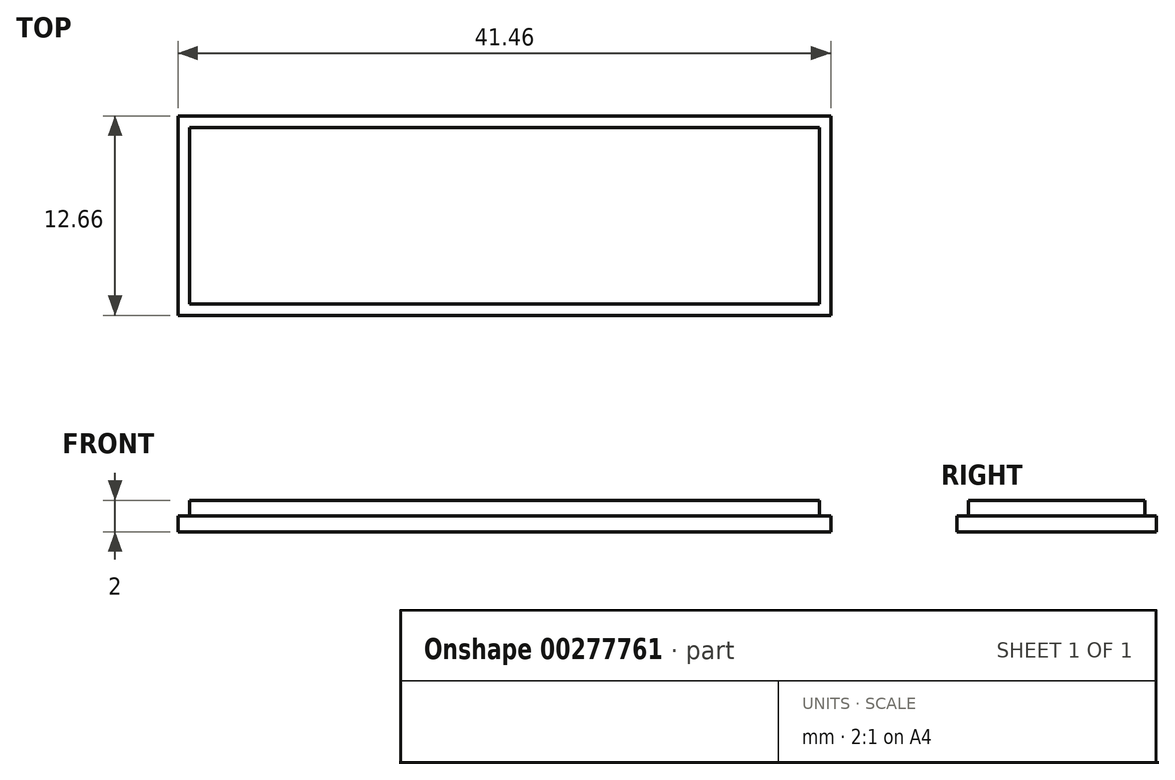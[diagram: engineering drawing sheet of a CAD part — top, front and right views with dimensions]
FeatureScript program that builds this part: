
annotation { "Feature Type Name" : "Feature", "Feature Type Description" : "" }
export const myFeature = defineFeature(function(context is Context, id is Id, definition is map)
    precondition{}
    {
        {
            var Q0;
            Q0=qCreatedBy(makeId("Top.planeOp"),FACE);
            var sketch = newSketch(context, id + "F0", { "sketchPlane" : qUnion([Q0])});
            skLineSegment(sketch, "E0.bottom", {"start": v(20.73, -6.33) * mm, "end": v(-20.73, -6.33) * mm});
            skLineSegment(sketch, "E0.top", {"start": v(20.73, 6.33) * mm, "end": v(-20.73, 6.33) * mm});
            skLineSegment(sketch, "E0.left", {"start": v(20.73, -6.33) * mm, "end": v(20.73, 6.33) * mm});
            skLineSegment(sketch, "E0.right", {"start": v(-20.73, -6.33) * mm, "end": v(-20.73, 6.33) * mm});
            skPoint(sketch, "E0.middle", {"position": v(0, 0) * mm});
            skSolve(sketch);
        }
        {
            var Q0;
            Q0 = qSketchRegion(id + "F0", true);
            extrude(context, id + "F1", {"entities" : qUnion([Q0]), "depth" : 1 * mm});
        }
        {
            var Q0;
            Q0=makeQuery(id+"F1.opExtrude","CAP_FACE",FACE,{"disambiguationData":[OSD([sQuery(id+"F0.wireOp",EDGE,"E0.bottom"),sQuery(id+"F0.wireOp",EDGE,"E0.top"),sQuery(id+"F0.wireOp",EDGE,"E0.left"),sQuery(id+"F0.wireOp",EDGE,"E0.right")])],"isStart":false});
            var sketch = newSketch(context, id + "F2", { "sketchPlane" : qUnion([Q0])});
            skLineSegment(sketch, "E1.bottom", {"start": v(20, -5.6) * mm, "end": v(-20, -5.6) * mm});
            skLineSegment(sketch, "E1.top", {"start": v(20, 5.6) * mm, "end": v(-20, 5.6) * mm});
            skLineSegment(sketch, "E1.left", {"start": v(20, -5.6) * mm, "end": v(20, 5.6) * mm});
            skLineSegment(sketch, "E1.right", {"start": v(-20, -5.6) * mm, "end": v(-20, 5.6) * mm});
            skPoint(sketch, "E1.middle", {"position": v(0, 0) * mm});
            skSolve(sketch);
        }
        {
            var Q0;
            Q0=makeQuery(id+"F2.imprint","IMPRINT",FACE,{"disambiguationData":[TD([[makeQuery(id+"F2.imprint","IMPRINT",EDGE,{"derivedFrom":sQuery(id+"F2.wireOp",EDGE,"E1.bottom")}),-1.0]])]});
            extrude(context, id + "F3", {"entities" : qUnion([Q0]), "operationType" : NewBodyOperationType.ADD, "depth" : 1 * mm});
        }
    });
